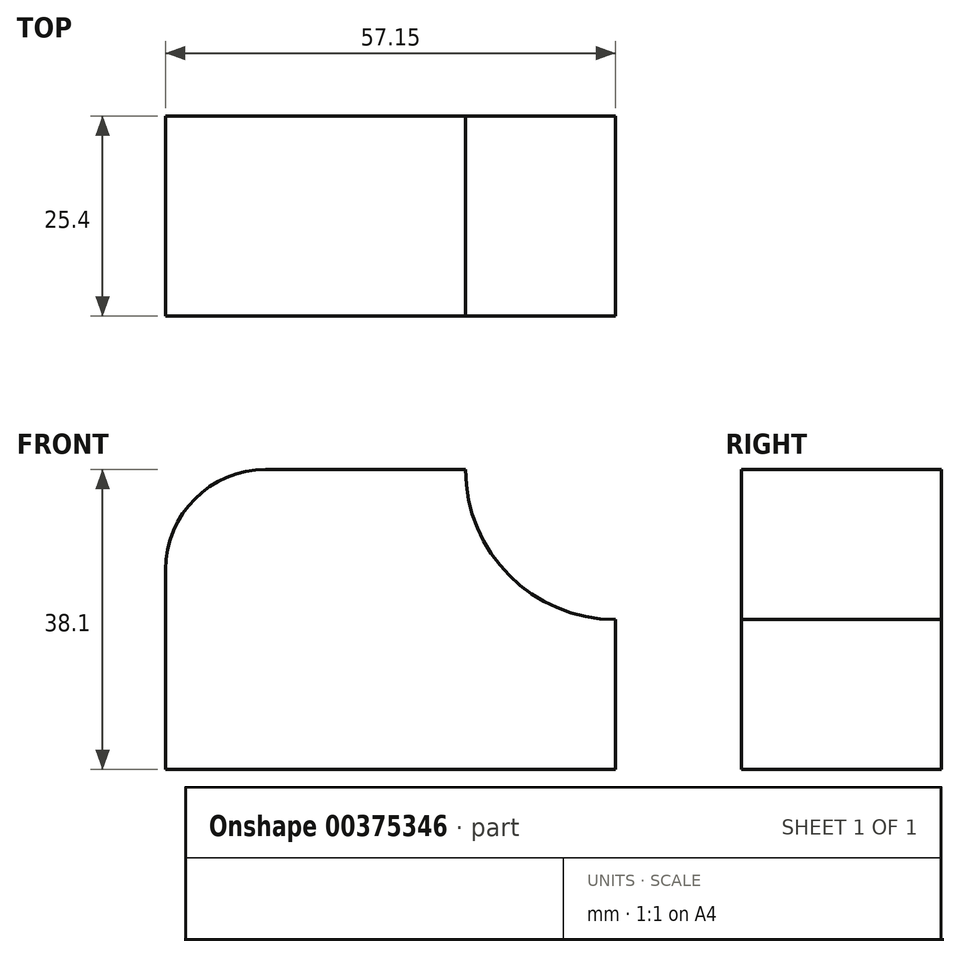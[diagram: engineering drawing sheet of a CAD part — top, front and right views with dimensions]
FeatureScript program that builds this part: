
annotation { "Feature Type Name" : "Feature", "Feature Type Description" : "" }
export const myFeature = defineFeature(function(context is Context, id is Id, definition is map)
    precondition{}
    {
        {
            var Q0;
            Q0=qCreatedBy(makeId("Front.planeOp"),FACE);
            var sketch = newSketch(context, id + "F0", { "sketchPlane" : qUnion([Q0])});
            skLineSegment(sketch, "E0", {"start": v(0, 0) * mm, "end": v(0, 38.1) * mm});
            skLineSegment(sketch, "E1", {"start": v(0, 38.1) * mm, "end": v(57.15, 38.1) * mm});
            skLineSegment(sketch, "E2", {"start": v(57.15, 38.1) * mm, "end": v(57.15, 0) * mm});
            skLineSegment(sketch, "E3", {"start": v(57.15, 0) * mm, "end": v(0, 0) * mm});
            skSolve(sketch);
        }
        {
            var Q0;
            Q0 = qSketchRegion(id + "F0", true);
            extrude(context, id + "F1", {"entities" : qUnion([Q0]), "depth" : 25.4 * mm});
        }
        {
            var Q0;
            Q0=makeQuery(id+"F1.opExtrude","SWEPT_EDGE",EDGE,{"disambiguationData":[OSD([sQuery(id+"F0.wireOp",EDGE,"E0"),sQuery(id+"F0.wireOp",EDGE,"E1")])]});
            fillet(context, id + "F2", {"entities" : qUnion([Q0]), "radius" : 12.7 * mm, "tangentPropagation" : true, "allowEdgeOverflow" : false});
        }
        {
            var Q0;
            Q0=makeQuery(id+"F1.opExtrude","CAP_FACE",FACE,{"disambiguationData":[OSD([sQuery(id+"F0.wireOp",EDGE,"E0"),sQuery(id+"F0.wireOp",EDGE,"E1"),sQuery(id+"F0.wireOp",EDGE,"E2"),sQuery(id+"F0.wireOp",EDGE,"E3")])],"isStart":false});
            var sketch = newSketch(context, id + "F3", { "sketchPlane" : qUnion([Q0])});
            skCircle(sketch, "E4", {"center": v(57.15, 38.1) * mm, "radius": 19.05 * mm});
            skSolve(sketch);
        }
        {
            var Q0;
            Q0 = qSketchRegion(id + "F3", true);
            extrude(context, id + "F4", {"entities" : qUnion([Q0]), "operationType" : NewBodyOperationType.REMOVE, "oppositeDirection" : true, "depth" : 25.4 * mm});
        }
    });
